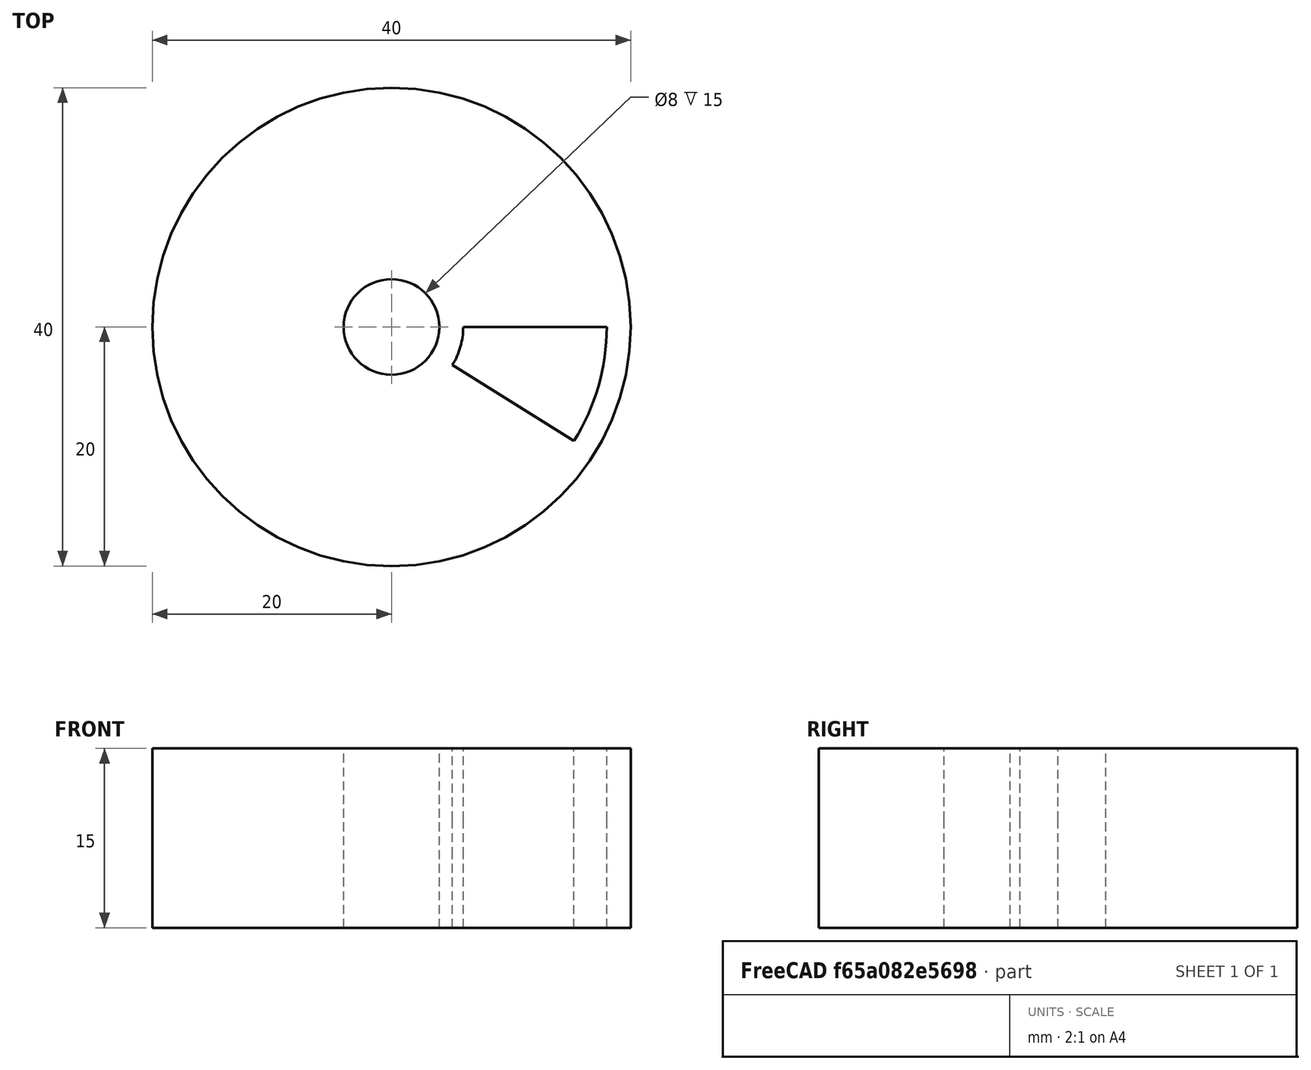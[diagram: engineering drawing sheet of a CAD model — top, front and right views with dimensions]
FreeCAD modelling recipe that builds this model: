
FCSTD DOCUMENT  (FreeCAD 0.14R3700 (Git))
Label: compartimentopastilladesalidav1
License: CC-BY 3.0
LicenseURL: http://creativecommons.org/licenses/by/3.0/
objects: Part::Cut×8, Part::MultiCommon×6, Part::Cylinder×4, Part::MultiFuse×1
note: 19 computed .brp shape members not serialized (recipe doc carries the construction recipe); baked Part::Feature solids carry a one-line shape summary decoded from their .brp

FEATURE [Part::Cylinder] Cylinder
  Angle = 360
  Height = 15
  Radius = 20
FEATURE [Part::Cylinder] Cylinder002
  Angle = 360
  Height = 20
  Radius = 6
FEATURE [Part::Cylinder] Cylinder003
  Angle = 360
  Height = 20
  Radius = 4
FEATURE [Part::Cut] Cut005
  Placement = pos=(0,0,-25) rot=(0,0,-1;0.453786rad)
FEATURE [Part::Cut] Cut006
  Placement = pos=(0,0,-25) rot=(0,0,1;3.64774rad)
FEATURE [Part::MultiCommon] Common003
  Placement = pos=(0,0,2) rot=(0,0,-1;2.07694rad)
  Shapes = -> [Cut006,Cut005]
FEATURE [Part::Cut] Cut007
  Placement = pos=(0,0,-25) rot=(0,0,-1;0.453786rad)
FEATURE [Part::Cut] Cut008
  Placement = pos=(0,0,-25) rot=(0,0,1;3.64774rad)
FEATURE [Part::MultiCommon] Common004
  Placement = pos=(0,0,2) rot=(0,0,-1;1.67552rad)
  Shapes = -> [Cut008,Cut007]
FEATURE [Part::MultiCommon] Common005
  Placement = pos=(0,0,1) rot=(0,0,1;0rad)
  Shapes = -> [Common004,Common003]
FEATURE [Part::MultiCommon] Common006
  Placement = pos=(0,0,2) rot=(0,0,-1;2.07694rad)
  Shapes = -> [Cut006,Cut005]
FEATURE [Part::MultiCommon] Common007
  Placement = pos=(0,0,2) rot=(0,0,-1;1.67552rad)
  Shapes = -> [Cut008,Cut007]
FEATURE [Part::MultiCommon] Common
  Placement = pos=(0,0,8) rot=(0,0,1;0rad)
  Shapes = -> [Common007,Common006]
FEATURE [Part::Cut] Cut
  Base = -> Cylinder
  Tool = -> Common
FEATURE [Part::Cut] Cut009
  Base = -> Cut
  Tool = -> Common005
FEATURE [Part::MultiFuse] Fusion
  Shapes = -> [Cylinder002,Cut009]
FEATURE [Part::Cut] Cut010
  Base = -> Fusion
  Tool = -> Cylinder003
FEATURE [Part::Cylinder] Cylinder004
  Angle = 360
  Height = 10
  Placement = pos=(0,0,15) rot=(0,0,1;0rad)
  Radius = 22
FEATURE [Part::Cut] Cut011
  Base = -> Cut010
  Tool = -> Cylinder004
